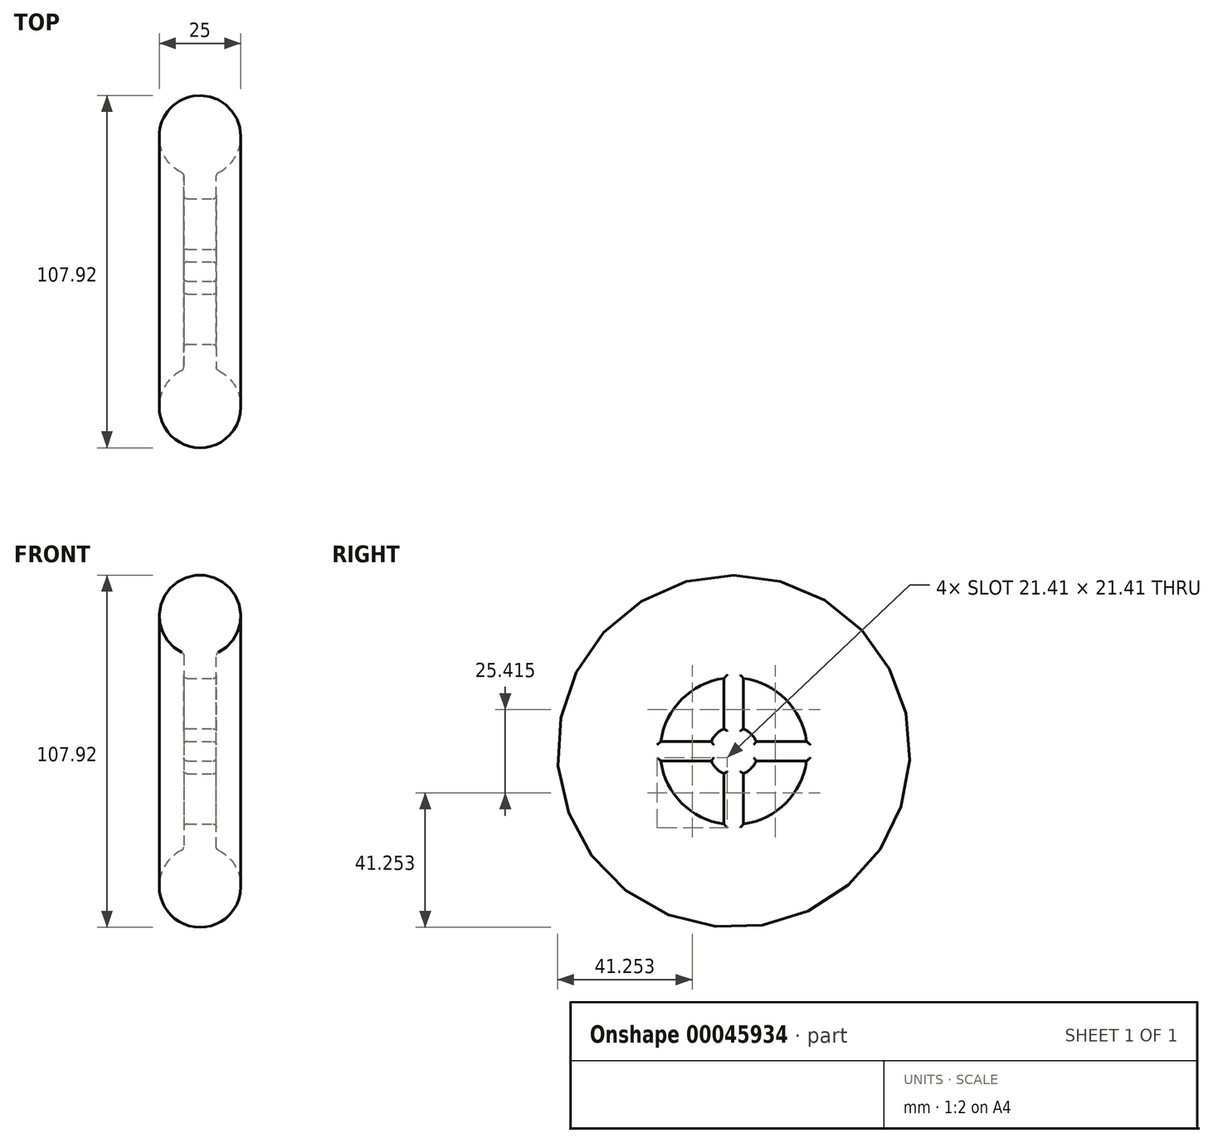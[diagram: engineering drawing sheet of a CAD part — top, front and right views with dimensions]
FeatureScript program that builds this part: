
annotation { "Feature Type Name" : "Feature", "Feature Type Description" : "" }
export const myFeature = defineFeature(function(context is Context, id is Id, definition is map)
    precondition{}
    {
        {
            var Q0;
            Q0=qCreatedBy(makeId("Front.planeOp"),FACE);
            var sketch = newSketch(context, id + "F0", { "sketchPlane" : qUnion([Q0])});
            skLineSegment(sketch, "E0", {"start": v(-10, 0) * mm, "end": v(-10, 30) * mm});
            skLineSegment(sketch, "E1", {"start": v(-10, 30) * mm, "end": v(0, 30) * mm});
            skLineSegment(sketch, "E2", {"start": v(0, 30) * mm, "end": v(0, 0) * mm});
            skLineSegment(sketch, "E3", {"start": v(0, 0) * mm, "end": v(-10, 0) * mm});
            skArc(sketch, "E4", {"start": v(0, 30) * mm, "mid": v(-5, 53.96) * mm, "end": v(-10, 30) * mm});
            skLineSegment(sketch, "E5", {"start": v(-73.27, 0) * mm, "end": v(55.82, 0) * mm});
            skSolve(sketch);
        }
        {
            var Q0;
            Q0=makeQuery(id+"F0.imprint","IMPRINT",FACE,{"disambiguationData":[TD([[makeQuery(id+"F0.imprint","IMPRINT",EDGE,{"derivedFrom":sQuery(id+"F0.wireOp",EDGE,"E0")}),-1.0]])]});
            var Q1;
            Q1=makeQuery(id+"F0.imprint","IMPRINT",FACE,{"disambiguationData":[TD([[makeQuery(id+"F0.imprint","IMPRINT",EDGE,{"derivedFrom":sQuery(id+"F0.wireOp",EDGE,"E1")}),1.0]])]});
            var Q2;
            Q2=sQuery(id+"F0.wireOp",EDGE,"E5");
            revolve(context, id + "F1", {"entities" : qUnion([Q0, Q1]), "axis" : qUnion([Q2]), "revolveType" : RevolveType.FULL});
        }
        {
            var Q0;
            Q0=qCreatedBy(makeId("Right.planeOp"),FACE);
            var sketch = newSketch(context, id + "F2", { "sketchPlane" : qUnion([Q0])});
            skArc(sketch, "E6", {"start": v(-3, 22.3) * mm, "mid": v(-15.9, 15.9) * mm, "end": v(-22.3, 3) * mm});
            skLineSegment(sketch, "E7", {"start": v(-22.3, 3) * mm, "end": v(-6.87, 3) * mm});
            skLineSegment(sketch, "E8", {"start": v(-3, 22.3) * mm, "end": v(-3, 6.87) * mm});
            skPoint(sketch, "E9.orphan", {"position": v(-63.4, 3) * mm});
            skPoint(sketch, "E10.orphan", {"position": v(-3, 57.37) * mm});
            skArc(sketch, "E11.trimOffspring", {"start": v(-3, 6.87) * mm, "mid": v(-5.3, 5.3) * mm, "end": v(-6.87, 3) * mm});
            skArc(sketch, "E12.1.0", {"start": v(-22.3, -3) * mm, "mid": v(-15.9, -15.9) * mm, "end": v(-3, -22.3) * mm});
            skLineSegment(sketch, "E12.1.1", {"start": v(-22.3, -3) * mm, "end": v(-6.87, -3) * mm});
            skLineSegment(sketch, "E12.1.2", {"start": v(-3, -22.3) * mm, "end": v(-3, -6.87) * mm});
            skArc(sketch, "E12.1.3", {"start": v(-6.87, -3) * mm, "mid": v(-5.3, -5.3) * mm, "end": v(-3, -6.87) * mm});
            skArc(sketch, "E12.2.0", {"start": v(3, -22.3) * mm, "mid": v(15.9, -15.9) * mm, "end": v(22.3, -3) * mm});
            skLineSegment(sketch, "E12.2.1", {"start": v(3, -22.3) * mm, "end": v(3, -6.87) * mm});
            skLineSegment(sketch, "E12.2.2", {"start": v(22.3, -3) * mm, "end": v(6.87, -3) * mm});
            skArc(sketch, "E12.2.3", {"start": v(3, -6.87) * mm, "mid": v(5.3, -5.3) * mm, "end": v(6.87, -3) * mm});
            skArc(sketch, "E12.3.0", {"start": v(22.3, 3) * mm, "mid": v(15.9, 15.9) * mm, "end": v(3, 22.3) * mm});
            skLineSegment(sketch, "E12.3.1", {"start": v(22.3, 3) * mm, "end": v(6.87, 3) * mm});
            skLineSegment(sketch, "E12.3.2", {"start": v(3, 22.3) * mm, "end": v(3, 6.87) * mm});
            skArc(sketch, "E12.3.3", {"start": v(6.87, 3) * mm, "mid": v(5.3, 5.3) * mm, "end": v(3, 6.87) * mm});
            skSolve(sketch);
        }
        {
            var Q0;
            Q0=makeQuery(id+"F2.imprint","IMPRINT",FACE,{"disambiguationData":[TD([[makeQuery(id+"F2.imprint","IMPRINT",EDGE,{"derivedFrom":sQuery(id+"F2.wireOp",EDGE,"E6")}),1.0]])]});
            var Q1;
            Q1=makeQuery(id+"F2.imprint","IMPRINT",FACE,{"disambiguationData":[TD([[makeQuery(id+"F2.imprint","IMPRINT",EDGE,{"derivedFrom":sQuery(id+"F2.wireOp",EDGE,"E12.3.0")}),1.0]])]});
            var Q2;
            Q2=makeQuery(id+"F2.imprint","IMPRINT",FACE,{"disambiguationData":[TD([[makeQuery(id+"F2.imprint","IMPRINT",EDGE,{"derivedFrom":sQuery(id+"F2.wireOp",EDGE,"E12.2.0")}),1.0]])]});
            var Q3;
            Q3=makeQuery(id+"F2.imprint","IMPRINT",FACE,{"disambiguationData":[TD([[makeQuery(id+"F2.imprint","IMPRINT",EDGE,{"derivedFrom":sQuery(id+"F2.wireOp",EDGE,"E12.1.0")}),1.0]])]});
            extrude(context, id + "F3", {"entities" : qUnion([Q0, Q1, Q2, Q3]), "operationType" : NewBodyOperationType.REMOVE, "oppositeDirection" : true, "depth" : 25 * mm});
        }
        {
            var Q0;
            Q0=makeQuery(id+"F1.opRevolve","SWEPT_FACE",FACE,{"disambiguationData":[OSD([sQuery(id+"F0.wireOp",EDGE,"E2")])]});
            fillet(context, id + "F4", {"entities" : qUnion([Q0]), "radius" : 1 * mm, "tangentPropagation" : true, "allowEdgeOverflow" : false});
        }
        {
            var Q0;
            Q0=makeQuery(id+"F1.opRevolve","SWEPT_FACE",FACE,{"disambiguationData":[OSD([sQuery(id+"F0.wireOp",EDGE,"E0")])]});
            fillet(context, id + "F5", {"entities" : qUnion([Q0]), "radius" : 1 * mm, "tangentPropagation" : true, "allowEdgeOverflow" : false});
        }
    });
